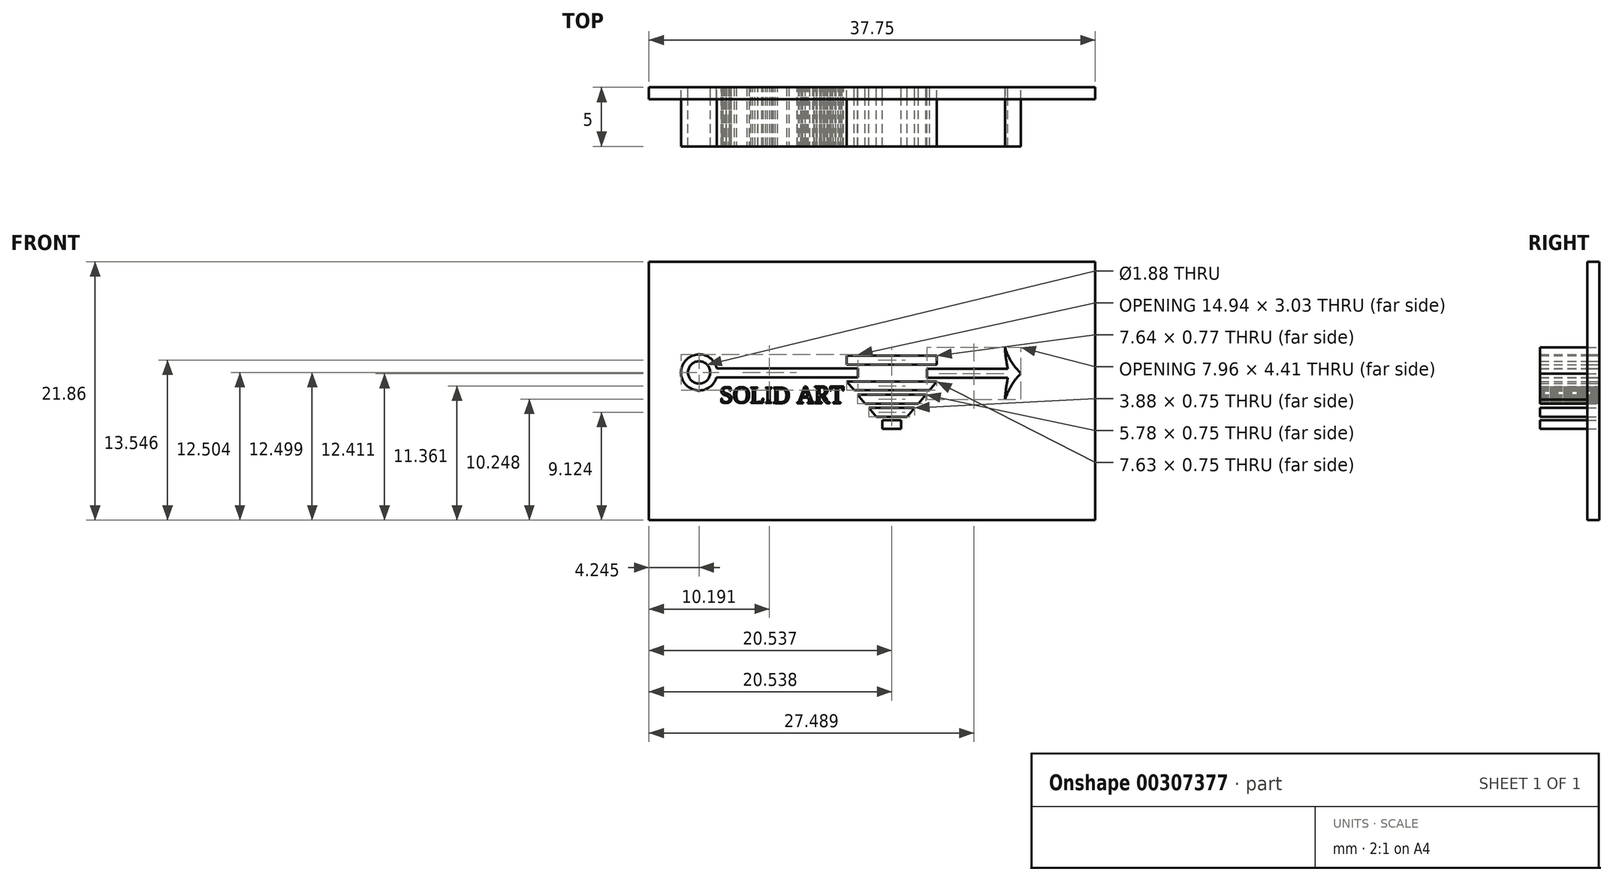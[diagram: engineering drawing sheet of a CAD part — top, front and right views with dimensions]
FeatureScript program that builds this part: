
annotation { "Feature Type Name" : "Feature", "Feature Type Description" : "" }
export const myFeature = defineFeature(function(context is Context, id is Id, definition is map)
    precondition{}
    {
        {
            var Q0;
            Q0=qCreatedBy(makeId("Front.planeOp"),FACE);
            var sketch = newSketch(context, id + "F0", { "sketchPlane" : qUnion([Q0])});
            skLineSegment(sketch, "E0", {"start": v(-14.18, -0.02) * mm, "end": v(-14.18, 1.86) * mm, "construction": true});
            skCircle(sketch, "E1", {"center": v(-14.18, 0.92) * mm, "radius": 0.94 * mm});
            skArc(sketch, "E2", {"start": v(-12.69, 1.25) * mm, "mid": v(-15.7, 0.96) * mm, "end": v(-12.7, 0.5) * mm});
            skLineSegment(sketch, "E3", {"start": v(-12.7, 0.5) * mm, "end": v(-0.76, 0.5) * mm});
            skLineSegment(sketch, "E4", {"start": v(-0.76, 0.5) * mm, "end": v(-0.76, 1.25) * mm});
            skLineSegment(sketch, "E5", {"start": v(-0.76, 1.25) * mm, "end": v(-12.69, 1.25) * mm});
            skLineSegment(sketch, "E6.bottom", {"start": v(-1.7, 2.35) * mm, "end": v(5.93, 2.35) * mm});
            skLineSegment(sketch, "E6.top", {"start": v(-1.7, 1.58) * mm, "end": v(5.93, 1.58) * mm});
            skLineSegment(sketch, "E6.left", {"start": v(-1.7, 2.35) * mm, "end": v(-1.7, 1.58) * mm});
            skLineSegment(sketch, "E6.right", {"start": v(5.93, 2.35) * mm, "end": v(5.93, 1.58) * mm});
            skLineSegment(sketch, "E7.bottom", {"start": v(1.32, -3.11) * mm, "end": v(2.9, -3.11) * mm});
            skLineSegment(sketch, "E7.top", {"start": v(1.32, -3.86) * mm, "end": v(2.9, -3.86) * mm});
            skLineSegment(sketch, "E7.left", {"start": v(1.32, -3.11) * mm, "end": v(1.32, -3.86) * mm});
            skLineSegment(sketch, "E7.right", {"start": v(2.9, -3.11) * mm, "end": v(2.9, -3.86) * mm});
            skLineSegment(sketch, "E8", {"start": v(-1.7, 0.16) * mm, "end": v(5.93, 0.16) * mm});
            skLineSegment(sketch, "E9", {"start": v(5.93, 0.16) * mm, "end": v(5.3, -0.6) * mm});
            skLineSegment(sketch, "E10", {"start": v(5.3, -0.6) * mm, "end": v(-1.07, -0.6) * mm});
            skLineSegment(sketch, "E11", {"start": v(-1.07, -0.6) * mm, "end": v(-1.7, 0.16) * mm});
            skLineSegment(sketch, "E12", {"start": v(-0.77, -0.96) * mm, "end": v(5, -0.96) * mm});
            skLineSegment(sketch, "E13", {"start": v(5, -0.96) * mm, "end": v(4.37, -1.7) * mm});
            skLineSegment(sketch, "E14", {"start": v(4.37, -1.7) * mm, "end": v(-0.13, -1.7) * mm});
            skLineSegment(sketch, "E15", {"start": v(-0.13, -1.7) * mm, "end": v(-0.77, -0.96) * mm});
            skLineSegment(sketch, "E16", {"start": v(0.18, -2.08) * mm, "end": v(4.06, -2.08) * mm});
            skLineSegment(sketch, "E17", {"start": v(4.06, -2.08) * mm, "end": v(3.43, -2.83) * mm});
            skLineSegment(sketch, "E18", {"start": v(3.43, -2.83) * mm, "end": v(0.8, -2.83) * mm});
            skLineSegment(sketch, "E19", {"start": v(0.8, -2.83) * mm, "end": v(0.18, -2.08) * mm});
            skLineSegment(sketch, "E20", {"start": v(5.1, 0.47) * mm, "end": v(11.94, 0.47) * mm});
            skLineSegment(sketch, "E21", {"start": v(11.94, 1.22) * mm, "end": v(5.1, 1.22) * mm});
            skLineSegment(sketch, "E22", {"start": v(5.1, 1.22) * mm, "end": v(5.1, 0.47) * mm});
            skFitSpline(sketch, "E23", {"points": [v(11.94, 0.47) * mm, v(11.7, -1.38) * mm], "startDerivative": vector(-0.05, -0.18) * mm, "endDerivative": vector(0, -1.95) * mm});
            skFitSpline(sketch, "E24", {"points": [v(11.7, -1.38) * mm, v(13.05, 0.83) * mm], "startDerivative": vector(0.88, 2.48) * mm, "endDerivative": vector(2.06, 1.9) * mm});
            skFitSpline(sketch, "E25", {"points": [v(13.05, 0.83) * mm, v(11.7, 3.04) * mm], "startDerivative": vector(-2.55, 2.47) * mm, "endDerivative": vector(-0.49, 1.75) * mm});
            skFitSpline(sketch, "E26", {"points": [v(11.94, 1.22) * mm, v(11.7, 3.04) * mm], "startDerivative": vector(-0.38, 1.9) * mm, "endDerivative": vector(0.01, 1.9) * mm});
            skLineSegment(sketch, "E27.bottom", {"start": v(-18.42, 10.28) * mm, "end": v(19.33, 10.28) * mm});
            skLineSegment(sketch, "E27.top", {"start": v(-18.42, -11.58) * mm, "end": v(19.33, -11.58) * mm});
            skLineSegment(sketch, "E27.left", {"start": v(-18.42, 10.28) * mm, "end": v(-18.42, -11.58) * mm});
            skLineSegment(sketch, "E27.right", {"start": v(19.33, 10.28) * mm, "end": v(19.33, -11.58) * mm});
            skSolve(sketch);
        }
        {
            var Q0;
            Q0=qCreatedBy(makeId("Front.planeOp"),FACE);
            var sketch = newSketch(context, id + "F1", { "sketchPlane" : qUnion([Q0])});
            skText(sketch, "E28", { "text": "SOLID", "fontName": "Tinos-Regular.ttf"});
            skText(sketch, "E29", { "text": "ART", "fontName": "NotoSerif-Regular.ttf"});
            const initialGuessF1  = {"E28": [-0.01244, -0.00164, 0.99997, -0.00783, 0.00145], "E29": [-0.00588, -0.00169, 1, 0, 0.00145]};
            skSetInitialGuess(sketch, initialGuessF1);
            skSolve(sketch);
        }
        {
            var Q0;
            Q0=makeQuery(id+"F0.imprint","IMPRINT",FACE,{"disambiguationData":[TD([[makeQuery(id+"F0.imprint","IMPRINT",EDGE,{"derivedFrom":sQuery(id+"F0.wireOp",EDGE,"E1")}),-1.0]])]});
            var Q1;
            Q1=makeQuery(id+"F0.imprint","IMPRINT",FACE,{"disambiguationData":[TD([[makeQuery(id+"F0.imprint","IMPRINT",EDGE,{"derivedFrom":sQuery(id+"F0.wireOp",EDGE,"E6.bottom")}),-1.0]])]});
            var Q2;
            Q2=makeQuery(id+"F0.imprint","IMPRINT",FACE,{"disambiguationData":[TD([[makeQuery(id+"F0.imprint","IMPRINT",EDGE,{"derivedFrom":sQuery(id+"F0.wireOp",EDGE,"E20")}),1.0]])]});
            var Q3;
            Q3=makeQuery(id+"F0.imprint","IMPRINT",FACE,{"disambiguationData":[TD([[makeQuery(id+"F0.imprint","IMPRINT",EDGE,{"derivedFrom":sQuery(id+"F0.wireOp",EDGE,"E8")}),-1.0]])]});
            var Q4;
            Q4=makeQuery(id+"F0.imprint","IMPRINT",FACE,{"disambiguationData":[TD([[makeQuery(id+"F0.imprint","IMPRINT",EDGE,{"derivedFrom":sQuery(id+"F0.wireOp",EDGE,"E12")}),-1.0]])]});
            var Q5;
            Q5=makeQuery(id+"F0.imprint","IMPRINT",FACE,{"disambiguationData":[TD([[makeQuery(id+"F0.imprint","IMPRINT",EDGE,{"derivedFrom":sQuery(id+"F0.wireOp",EDGE,"E16")}),-1.0]])]});
            var Q6;
            Q6=makeQuery(id+"F0.imprint","IMPRINT",FACE,{"disambiguationData":[TD([[makeQuery(id+"F0.imprint","IMPRINT",EDGE,{"derivedFrom":sQuery(id+"F0.wireOp",EDGE,"E7.bottom")}),-1.0]])]});
            var Q7;
            Q7 = qSketchRegion(id + "F1", true);
            extrude(context, id + "F2", {"entities" : qUnion([Q0, Q1, Q2, Q3, Q4, Q5, Q6, Q7]), "depth" : 5 * mm});
        }
        {
            var Q0;
            Q0 = qSketchRegion(id + "F0", true);
            var Q1;
            Q1=makeQuery(id+"F0.imprint","IMPRINT",FACE,{"disambiguationData":[TD([[makeQuery(id+"F0.imprint","IMPRINT",EDGE,{"derivedFrom":sQuery(id+"F0.wireOp",EDGE,"E1")}),1.0]])]});
            extrude(context, id + "F3", {"entities" : qUnion([Q0, Q1]), "depth" : 1 * mm});
        }
    });
